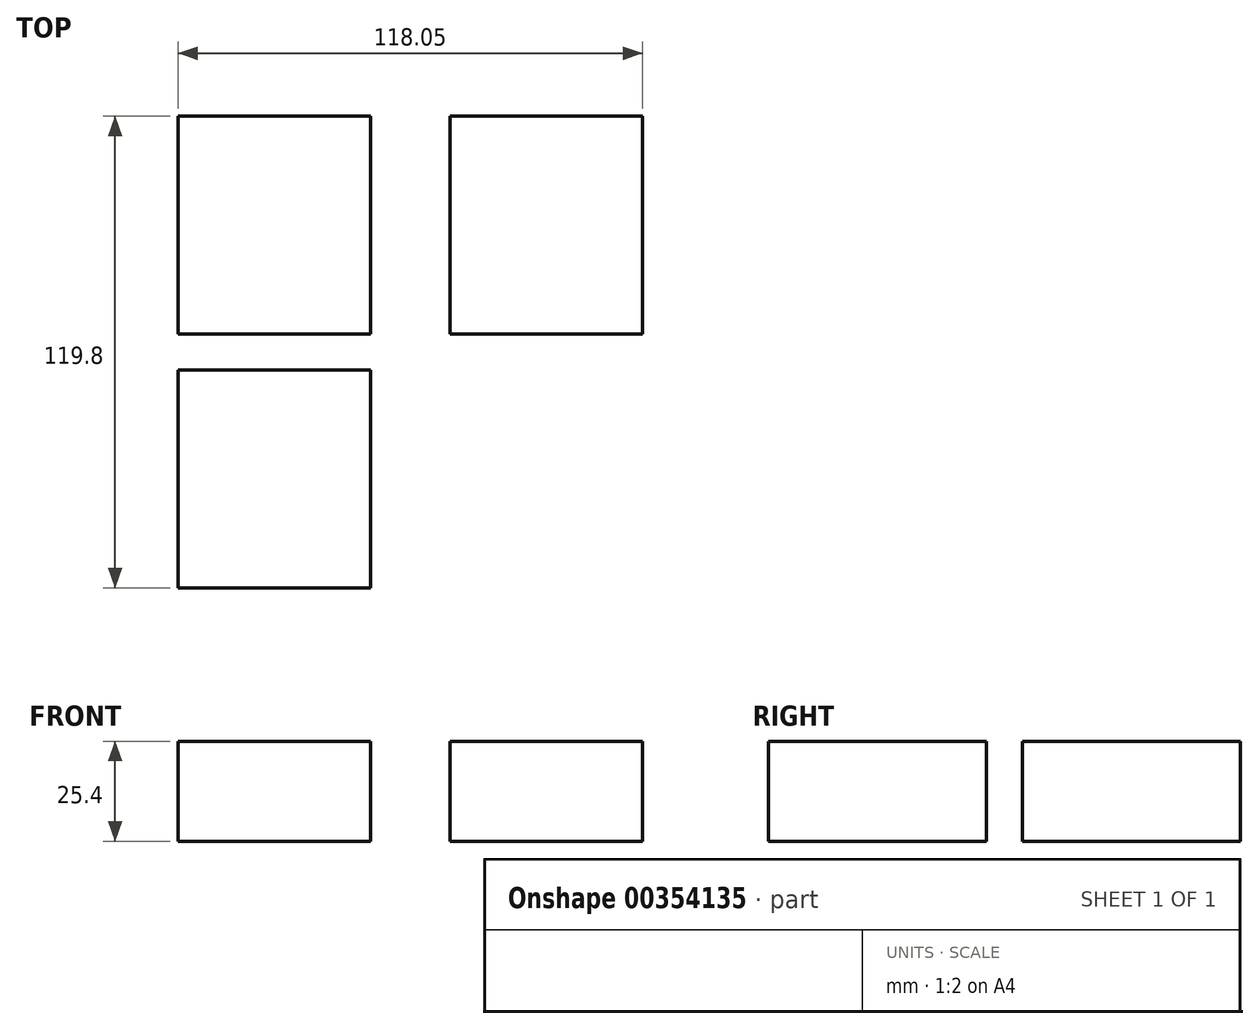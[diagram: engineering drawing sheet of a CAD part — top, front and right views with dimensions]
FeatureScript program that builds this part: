
annotation { "Feature Type Name" : "Feature", "Feature Type Description" : "" }
export const myFeature = defineFeature(function(context is Context, id is Id, definition is map)
    precondition{}
    {
        {
            var Q0;
            Q0=qCreatedBy(makeId("Top.planeOp"),FACE);
            var sketch = newSketch(context, id + "F0", { "sketchPlane" : qUnion([Q0])});
            skLineSegment(sketch, "E0.bottom", {"start": v(-63.25, 48.53) * mm, "end": v(-14.28, 48.53) * mm});
            skLineSegment(sketch, "E0.top", {"start": v(-63.25, -6.85) * mm, "end": v(-14.28, -6.85) * mm});
            skLineSegment(sketch, "E0.left", {"start": v(-63.25, 48.53) * mm, "end": v(-63.25, -6.85) * mm});
            skLineSegment(sketch, "E0.right", {"start": v(-14.28, 48.53) * mm, "end": v(-14.28, -6.85) * mm});
            skLineSegment(sketch, "E1.bottom", {"start": v(5.83, 48.53) * mm, "end": v(54.8, 48.53) * mm});
            skLineSegment(sketch, "E1.top", {"start": v(5.83, -6.85) * mm, "end": v(54.8, -6.85) * mm});
            skLineSegment(sketch, "E1.left", {"start": v(5.83, 48.53) * mm, "end": v(5.83, -6.85) * mm});
            skLineSegment(sketch, "E1.right", {"start": v(54.8, 48.53) * mm, "end": v(54.8, -6.85) * mm});
            skLineSegment(sketch, "E2.bottom", {"start": v(-63.25, -15.89) * mm, "end": v(-14.28, -15.89) * mm});
            skLineSegment(sketch, "E2.top", {"start": v(-63.25, -71.27) * mm, "end": v(-14.28, -71.27) * mm});
            skLineSegment(sketch, "E2.left", {"start": v(-63.25, -15.89) * mm, "end": v(-63.25, -71.27) * mm});
            skLineSegment(sketch, "E2.right", {"start": v(-14.28, -15.89) * mm, "end": v(-14.28, -71.27) * mm});
            skSolve(sketch);
        }
        {
            var Q0;
            Q0 = qSketchRegion(id + "F0", true);
            extrude(context, id + "F1", {"entities" : qUnion([Q0]), "depth" : 25.4 * mm});
        }
    });
